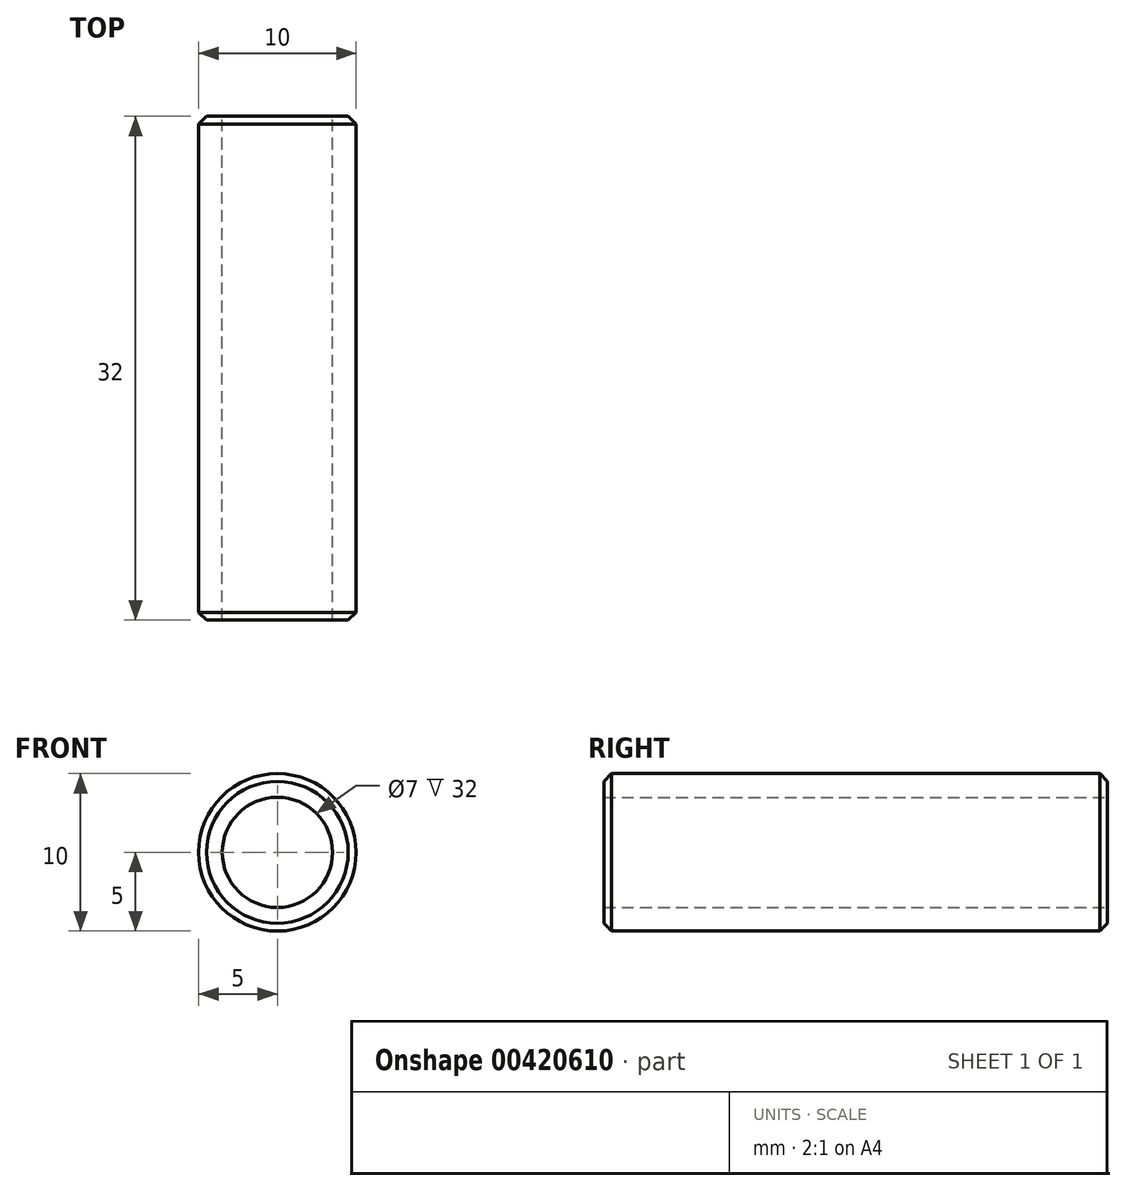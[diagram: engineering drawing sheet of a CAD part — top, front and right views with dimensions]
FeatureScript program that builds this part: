
annotation { "Feature Type Name" : "Feature", "Feature Type Description" : "" }
export const myFeature = defineFeature(function(context is Context, id is Id, definition is map)
    precondition{}
    {
        {
            var Q0;
            Q0=qCreatedBy(makeId("Front.planeOp"),FACE);
            var sketch = newSketch(context, id + "F0", { "sketchPlane" : qUnion([Q0])});
            skCircle(sketch, "E0", {"center": v(0, 0) * mm, "radius": 5 * mm});
            skCircle(sketch, "E1", {"center": v(0, 0) * mm, "radius": 3.5 * mm});
            skSolve(sketch);
        }
        {
            var Q0;
            Q0 = qSketchRegion(id + "F0", true);
            extrude(context, id + "F1", {"entities" : qUnion([Q0]), "depth" : 32 * mm, "offsetDistance" : 25 * mm, "symmetric" : true});
        }
        {
            var Q0;
            Q0=makeQuery(id+"F1.opExtrude","CAP_EDGE",EDGE,{"disambiguationData":[OSD([sQuery(id+"F0.wireOp",EDGE,"E0")])],"isStart":false});
            var Q1;
            Q1=makeQuery(id+"F1.opExtrude","CAP_EDGE",EDGE,{"disambiguationData":[OSD([sQuery(id+"F0.wireOp",EDGE,"E0")])],"isStart":true});
            chamfer(context, id + "F2", {"entities" : qUnion([Q0, Q1]), "width" : 0.5 * mm, "tangentPropagation" : true});
        }
    });
